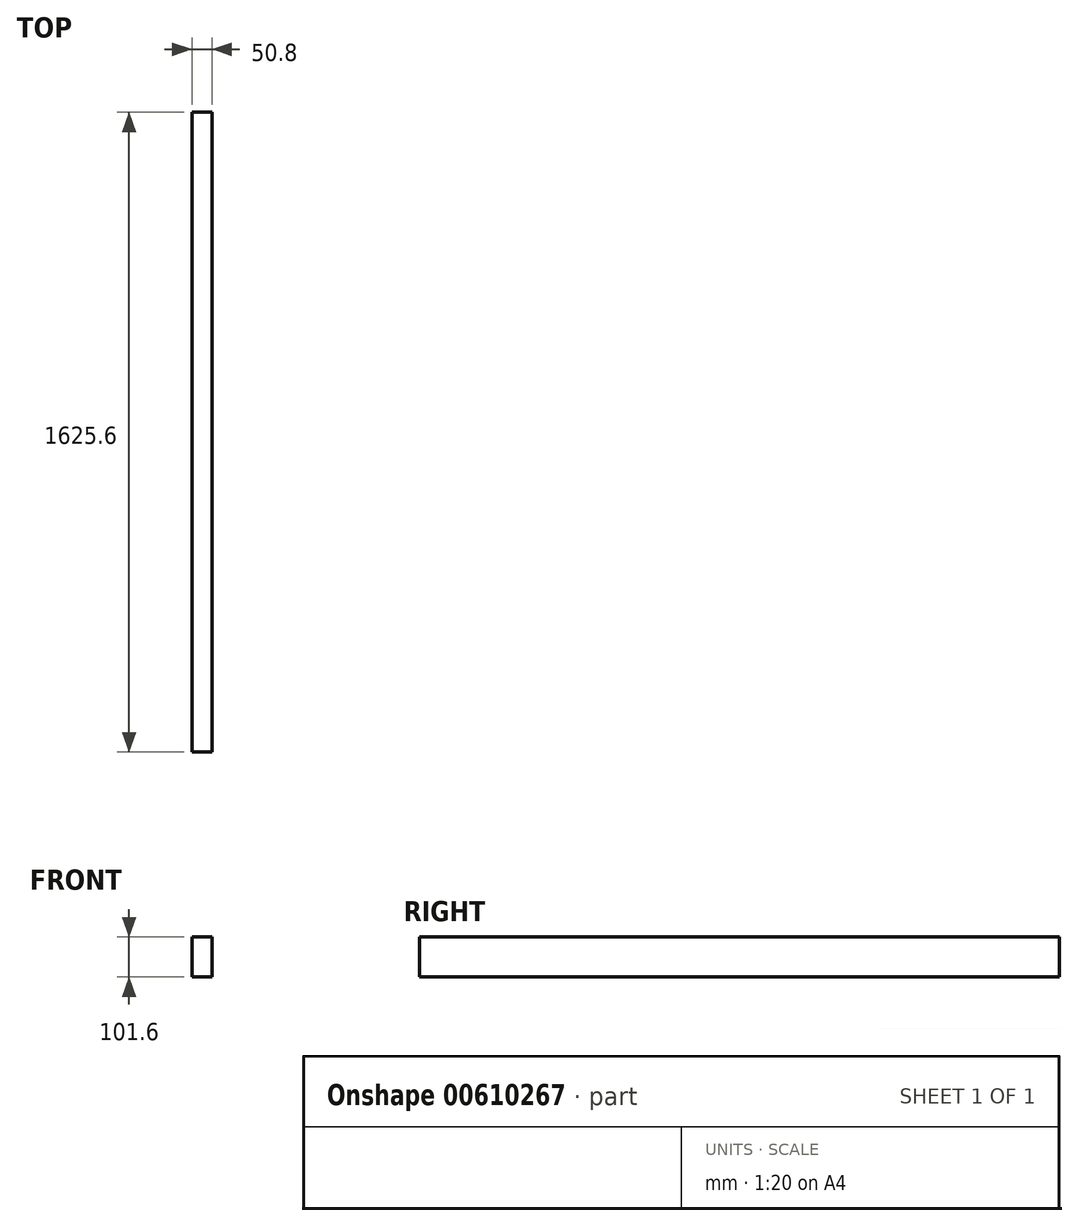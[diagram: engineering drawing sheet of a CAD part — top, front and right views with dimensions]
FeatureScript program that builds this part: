
annotation { "Feature Type Name" : "Feature", "Feature Type Description" : "" }
export const myFeature = defineFeature(function(context is Context, id is Id, definition is map)
    precondition{}
    {
        {
            var Q0;
            Q0=qCreatedBy(makeId("Front.planeOp"),FACE);
            var sketch = newSketch(context, id + "F0", { "sketchPlane" : qUnion([Q0])});
            skLineSegment(sketch, "E0.bottom", {"start": v(-25.4, 50.8) * mm, "end": v(25.4, 50.8) * mm});
            skLineSegment(sketch, "E0.top", {"start": v(-25.4, -50.8) * mm, "end": v(25.4, -50.8) * mm});
            skLineSegment(sketch, "E0.left", {"start": v(-25.4, 50.8) * mm, "end": v(-25.4, -50.8) * mm});
            skLineSegment(sketch, "E0.right", {"start": v(25.4, 50.8) * mm, "end": v(25.4, -50.8) * mm});
            skSolve(sketch);
        }
        {
            var Q0;
            Q0 = qSketchRegion(id + "F0", true);
            extrude(context, id + "F1", {"entities" : qUnion([Q0]), "depth" : 1625.6 * mm, "offsetDistance" : 25.4 * mm});
        }
    });
